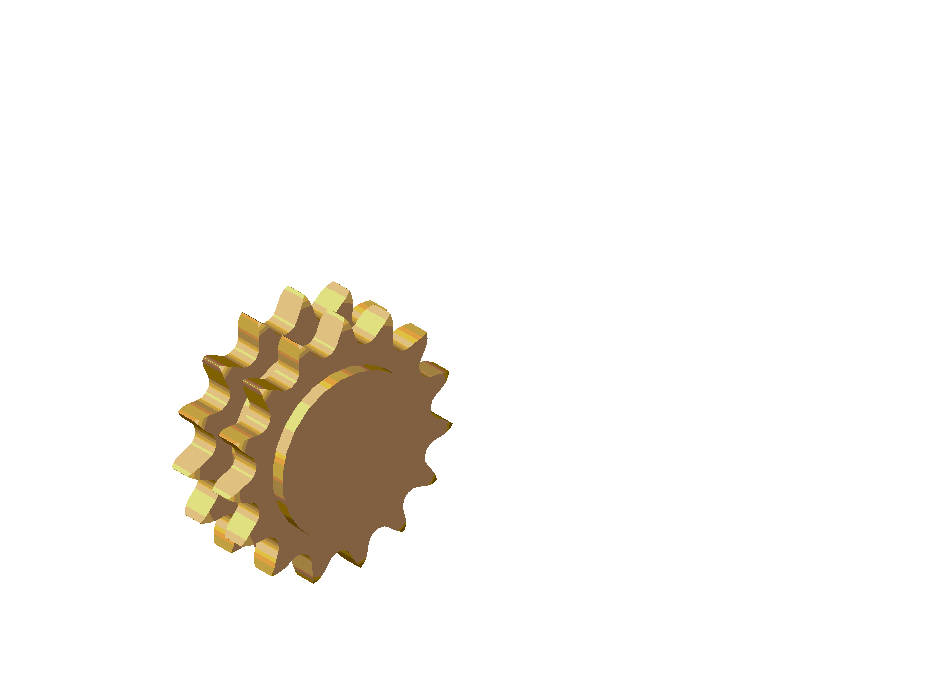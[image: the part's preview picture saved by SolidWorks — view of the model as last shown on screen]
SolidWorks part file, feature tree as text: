
SOLIDWORKS PART (.sldprt)
format: sldprt  version: not decoded by parser v0  size: 252,928 bytes
history: native  units: mm
features: sketch x2, pattern_circular x2, revolve x1, cut_extrude x1, pattern_linear x1, plane x1 (+9 scaffold rows collapsed)
feature tree (17):
  scaffold x9  (default folders/planes/origin — collapsed)
  sketch  "Sketch2"  dims[D1=16.6497mm D2=23.622mm D3=46.0mm D4=~129.910879mm D5=~207.069729mm D6=~2.778125mm]
  revolve  "Base-Revolve"  Angle=360deg
  sketch  "Sketch3"  dims[c1.D1=~183.250879mm c1.D4=~11.319626mm c1.D5=58.674mm c1.D6=~40.977601mm c1.D2=~63.79507mm c2.D2=124.0deg c2.D3=~63.79507mm c3.D3=62.0deg c3.D5=~50.496989mm]
  cut_extrude  "Cut-Extrude1"  [1 undecoded]
  pattern_circular  "CirPattern1"  Count=15 Angle=24deg
  pattern_linear  "LPattern1"  Count1=2 Count2=1 Spacing1=45.4406mm Spacing2=50mm
  plane  "Plane1"  Offset=399.313341mm
  pattern_circular  "AxisDistance"  [2 undecoded]
decode coverage: 5 of 7 modeling features carry decoded parameters
note: ~ marks probable driven/reference dimensions
note: 3 parameter values undecoded
note: suppression state not decoded; provenance and decode notes live in map.json
